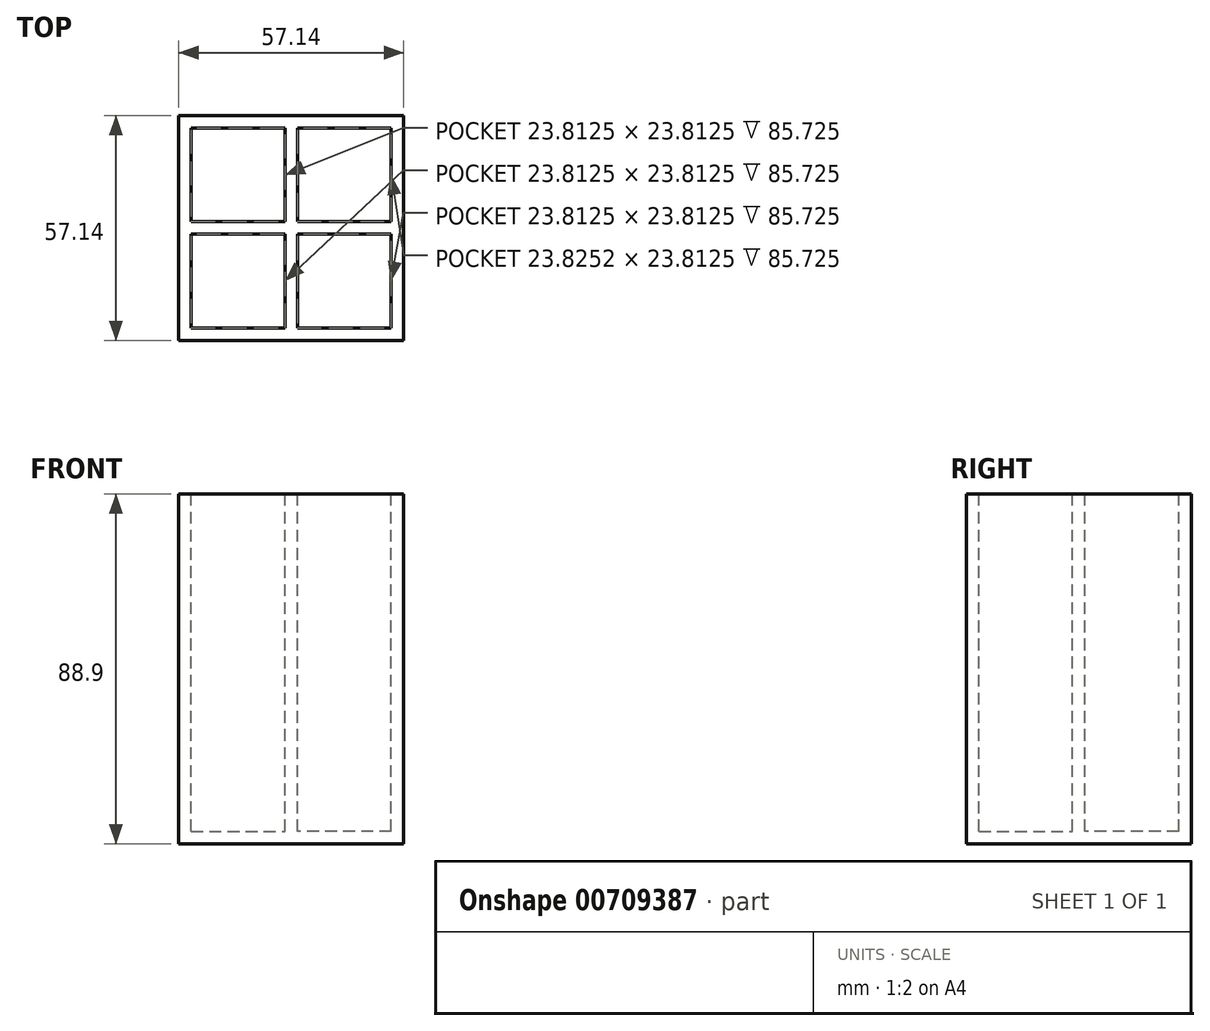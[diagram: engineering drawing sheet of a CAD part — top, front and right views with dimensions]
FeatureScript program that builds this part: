
annotation { "Feature Type Name" : "Feature", "Feature Type Description" : "" }
export const myFeature = defineFeature(function(context is Context, id is Id, definition is map)
    precondition{}
    {
        {
            var Q0;
            Q0=qCreatedBy(makeId("Top.planeOp"),FACE);
            var sketch = newSketch(context, id + "F0", { "sketchPlane" : qUnion([Q0])});
            skLineSegment(sketch, "E0.bottom", {"start": v(28.58, 28.58) * mm, "end": v(-28.57, 28.58) * mm});
            skLineSegment(sketch, "E0.top", {"start": v(28.57, -28.58) * mm, "end": v(-28.58, -28.58) * mm});
            skLineSegment(sketch, "E0.left", {"start": v(28.58, 28.58) * mm, "end": v(28.57, -28.58) * mm});
            skLineSegment(sketch, "E0.right", {"start": v(-28.57, 28.58) * mm, "end": v(-28.58, -28.58) * mm});
            skPoint(sketch, "E0.middle", {"position": v(0, 0) * mm});
            skSolve(sketch);
        }
        {
            var Q0;
            Q0 = qSketchRegion(id + "F0", true);
            extrude(context, id + "F1", {"entities" : qUnion([Q0]), "depth" : 88.9 * mm, "offsetDistance" : 25.4 * mm});
        }
        {
            var Q0;
            Q0=makeQuery(id+"F1.opExtrude","CAP_FACE",FACE,{"disambiguationData":[OSD([sQuery(id+"F0.wireOp",EDGE,"E0.bottom"),sQuery(id+"F0.wireOp",EDGE,"E0.top"),sQuery(id+"F0.wireOp",EDGE,"E0.left"),sQuery(id+"F0.wireOp",EDGE,"E0.right")])],"isStart":false});
            var sketch = newSketch(context, id + "F2", { "sketchPlane" : qUnion([Q0])});
            skLineSegment(sketch, "E1.bottom", {"start": v(-25.4, 25.4) * mm, "end": v(-1.59, 25.4) * mm});
            skLineSegment(sketch, "E1.top", {"start": v(-25.4, 1.59) * mm, "end": v(-1.59, 1.59) * mm});
            skLineSegment(sketch, "E1.left", {"start": v(-25.4, 25.4) * mm, "end": v(-25.4, 1.59) * mm});
            skLineSegment(sketch, "E1.right", {"start": v(-1.59, 25.4) * mm, "end": v(-1.59, 1.59) * mm});
            skLineSegment(sketch, "E2.bottom", {"start": v(-25.4, -25.4) * mm, "end": v(-1.59, -25.4) * mm});
            skLineSegment(sketch, "E2.top", {"start": v(-25.4, -1.59) * mm, "end": v(-1.59, -1.59) * mm});
            skLineSegment(sketch, "E2.left", {"start": v(-25.4, -25.4) * mm, "end": v(-25.4, -1.59) * mm});
            skLineSegment(sketch, "E2.right", {"start": v(-1.59, -25.4) * mm, "end": v(-1.59, -1.59) * mm});
            skLineSegment(sketch, "E3.bottom", {"start": v(25.4, -25.4) * mm, "end": v(1.59, -25.4) * mm});
            skLineSegment(sketch, "E3.top", {"start": v(25.4, -1.59) * mm, "end": v(1.59, -1.59) * mm});
            skLineSegment(sketch, "E3.left", {"start": v(25.4, -25.4) * mm, "end": v(25.4, -1.59) * mm});
            skLineSegment(sketch, "E3.right", {"start": v(1.59, -25.4) * mm, "end": v(1.59, -1.59) * mm});
            skLineSegment(sketch, "E4.bottom", {"start": v(25.4, 25.4) * mm, "end": v(1.57, 25.4) * mm});
            skLineSegment(sketch, "E4.top", {"start": v(25.4, 1.59) * mm, "end": v(1.57, 1.59) * mm});
            skLineSegment(sketch, "E4.left", {"start": v(25.4, 25.4) * mm, "end": v(25.4, 1.59) * mm});
            skLineSegment(sketch, "E4.right", {"start": v(1.57, 25.4) * mm, "end": v(1.57, 1.59) * mm});
            skSolve(sketch);
        }
        {
            var Q0;
            Q0 = qSketchRegion(id + "F2", true);
            extrude(context, id + "F3", {"entities" : qUnion([Q0]), "operationType" : NewBodyOperationType.REMOVE, "oppositeDirection" : true, "depth" : 85.72 * mm, "offsetDistance" : 25.4 * mm});
        }
    });
